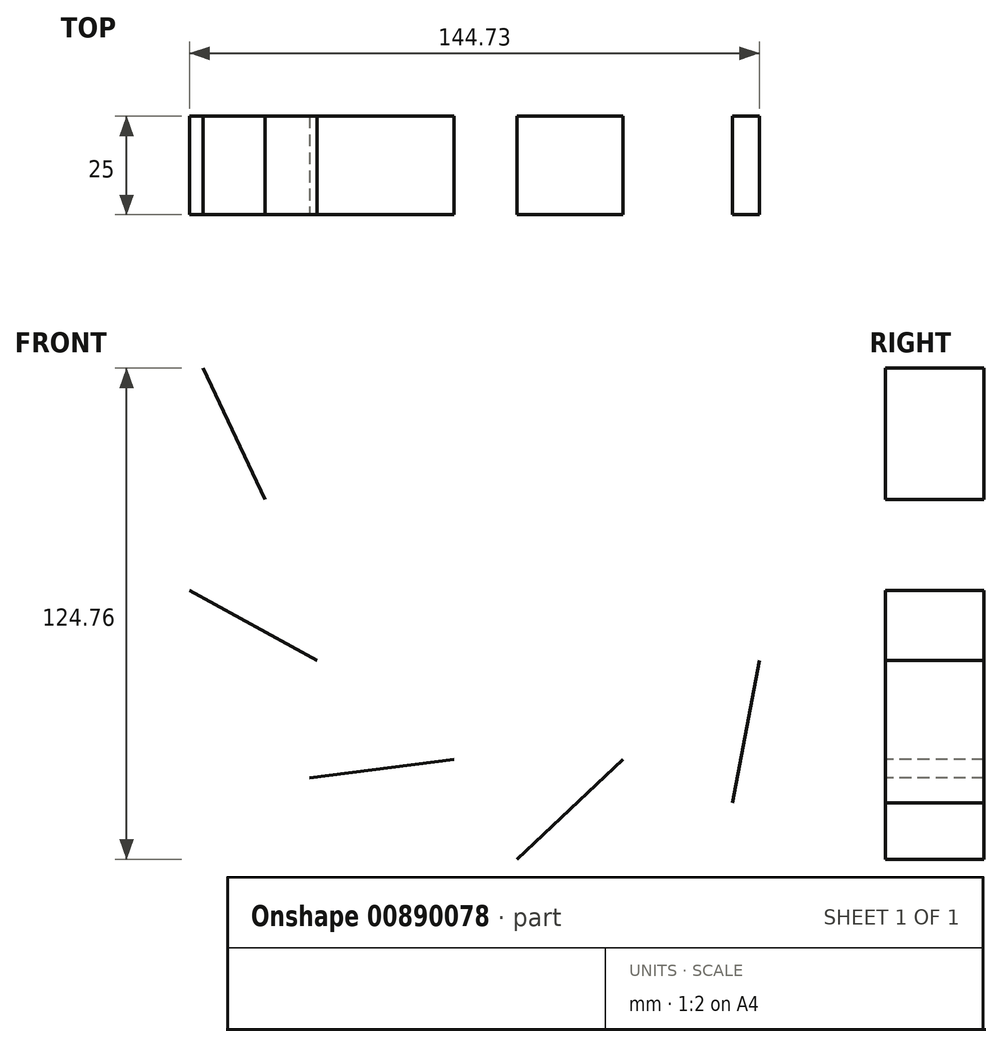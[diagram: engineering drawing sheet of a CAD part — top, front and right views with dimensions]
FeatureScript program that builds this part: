
annotation { "Feature Type Name" : "Feature", "Feature Type Description" : "" }
export const myFeature = defineFeature(function(context is Context, id is Id, definition is map)
    precondition{}
    {
        {
            var Q0;
            Q0=qCreatedBy(makeId("Front.planeOp"),FACE);
            var sketch = newSketch(context, id + "F0", { "sketchPlane" : qUnion([Q0])});
            skLineSegment(sketch, "E0", {"start": v(-69.42, 0) * mm, "end": v(-85.22, 33.39) * mm});
            skLineSegment(sketch, "E1.1.0", {"start": v(-56.16, -40.8) * mm, "end": v(-88.57, -23.08) * mm});
            skLineSegment(sketch, "E1.2.0", {"start": v(-21.45, -66.02) * mm, "end": v(-58.09, -70.73) * mm});
            skLineSegment(sketch, "E1.3.0", {"start": v(21.45, -66.02) * mm, "end": v(-5.42, -91.37) * mm});
            skLineSegment(sketch, "E1.4.0", {"start": v(56.16, -40.8) * mm, "end": v(49.32, -77.1) * mm});
            skPoint(sketch, "E1.center", {"position": v(0, 0) * mm});
            skLineSegment(sketch, "E2.1.5.0", {"start": v(69.42, 0) * mm, "end": v(85.22, -33.39) * mm});
            skLineSegment(sketch, "E2.1.6.0", {"start": v(56.16, 40.8) * mm, "end": v(88.57, 23.08) * mm});
            skLineSegment(sketch, "E2.1.7.0", {"start": v(21.45, 66.02) * mm, "end": v(58.09, 70.73) * mm});
            skLineSegment(sketch, "E2.1.8.0", {"start": v(-21.45, 66.02) * mm, "end": v(5.42, 91.37) * mm});
            skLineSegment(sketch, "E2.1.9.0", {"start": v(-56.16, 40.8) * mm, "end": v(-49.32, 77.1) * mm});
            skSolve(sketch);
        }
        {
            var Q0;
            Q0=sQuery(id+"F0.wireOp",EDGE,"E1.2.0");
            var Q1;
            Q1=sQuery(id+"F0.wireOp",EDGE,"E1.9.0");
            var Q2;
            Q2=sQuery(id+"F0.wireOp",EDGE,"E1.3.0");
            var Q3;
            Q3=sQuery(id+"F0.wireOp",EDGE,"E1.6.0");
            var Q4;
            Q4=sQuery(id+"F0.wireOp",EDGE,"E0");
            var Q5;
            Q5=sQuery(id+"F0.wireOp",EDGE,"E1.4.0");
            var Q6;
            Q6=sQuery(id+"F0.wireOp",EDGE,"E1.7.0");
            var Q7;
            Q7=sQuery(id+"F0.wireOp",EDGE,"E1.1.0");
            var Q8;
            Q8=sQuery(id+"F0.wireOp",EDGE,"E1.5.0");
            var Q9;
            Q9=sQuery(id+"F0.wireOp",EDGE,"E1.8.0");
            extrude(context, id + "F1", {"bodyType" : ToolBodyType.SURFACE, "surfaceEntities" : qUnion([Q0, Q1, Q2, Q3, Q4, Q5, Q6, Q7, Q8, Q9]), "depth" : 25 * mm, "offsetDistance" : 25 * mm});
        }
    });
